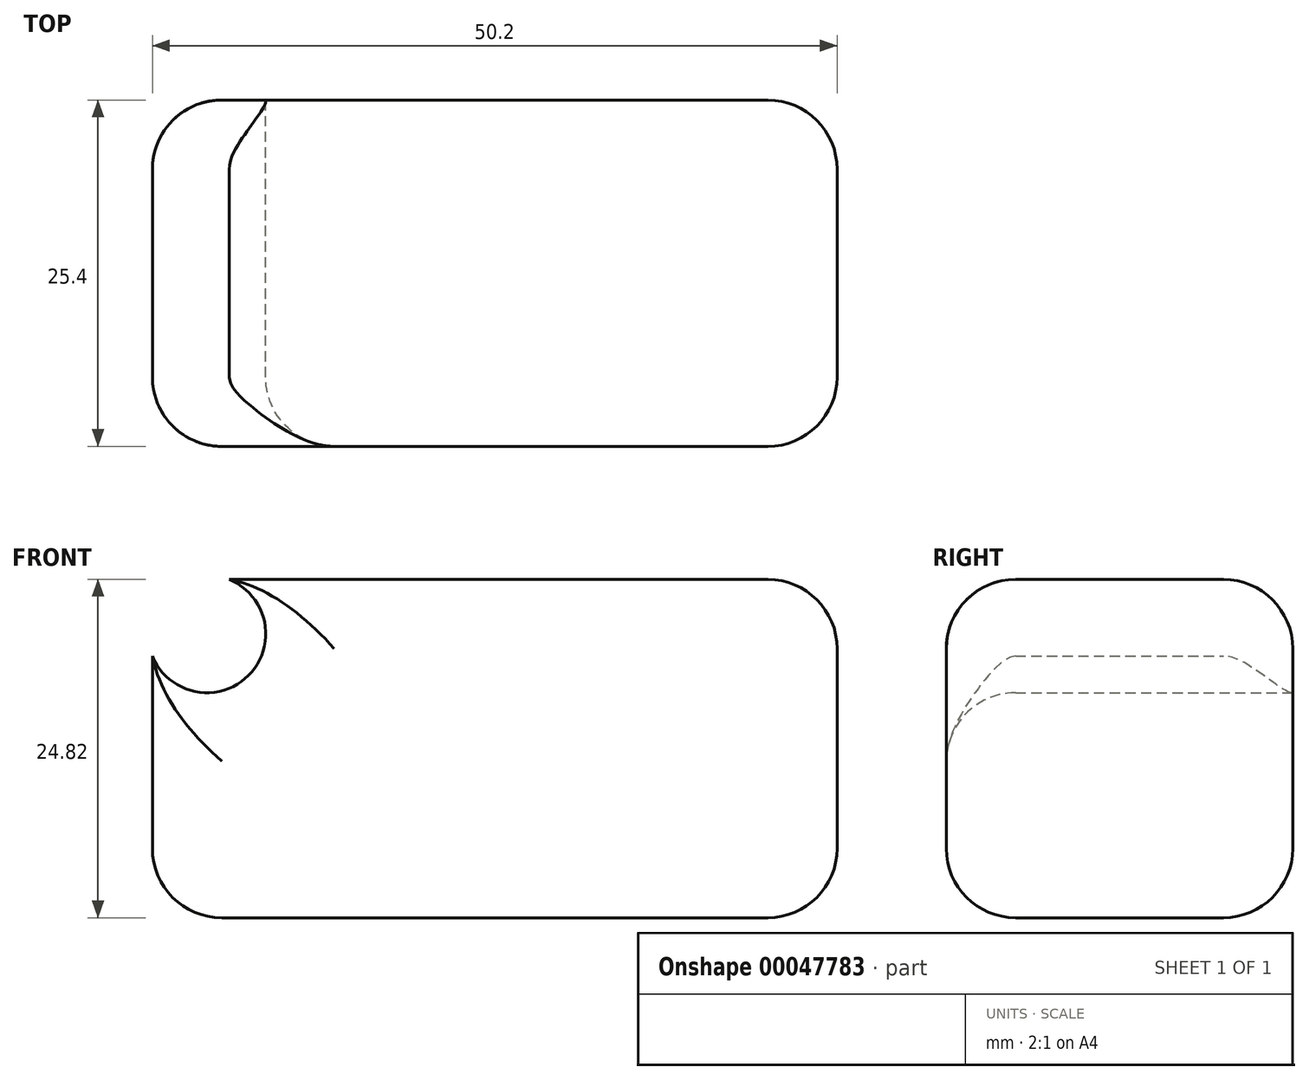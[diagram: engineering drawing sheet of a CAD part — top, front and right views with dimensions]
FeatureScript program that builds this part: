
annotation { "Feature Type Name" : "Feature", "Feature Type Description" : "" }
export const myFeature = defineFeature(function(context is Context, id is Id, definition is map)
    precondition{}
    {
        {
            var Q0;
            Q0=qCreatedBy(makeId("Front.planeOp"),FACE);
            var sketch = newSketch(context, id + "F0", { "sketchPlane" : qUnion([Q0])});
            skLineSegment(sketch, "E0.bottom", {"start": v(-47.06, 38.94) * mm, "end": v(3.14, 38.94) * mm});
            skLineSegment(sketch, "E0.top", {"start": v(-47.06, 14.12) * mm, "end": v(3.14, 14.12) * mm});
            skLineSegment(sketch, "E0.left", {"start": v(-47.06, 38.94) * mm, "end": v(-47.06, 14.12) * mm});
            skLineSegment(sketch, "E0.right", {"start": v(3.14, 38.94) * mm, "end": v(3.14, 14.12) * mm});
            skCircle(sketch, "E1", {"center": v(-43.07, 34.94) * mm, "radius": 4.32 * mm});
            skSolve(sketch);
        }
        {
            var Q0;
            {var subQ6=sQuery(id+"F0.wireOp",EDGE,"E0.top");Q0=makeQuery(id+"F0.imprint","IMPRINT",FACE,{"disambiguationData":[TD([[makeQuery(id+"F0.imprint","IMPRINT",EDGE,{"derivedFrom":subQ6}),1.0]])]});}
            extrude(context, id + "F1", {"entities" : qUnion([Q0]), "depth" : 25.4 * mm});
        }
        {
            var Q0;
            Q0=makeQuery(id+"F1.opExtrude","CAP_EDGE",EDGE,{"disambiguationData":[OSD([sQuery(id+"F0.wireOp",EDGE,"E0.bottom")])],"isStart":false});
            var Q1;
            Q1=makeQuery(id+"F1.opExtrude","CAP_FACE",FACE,{"disambiguationData":[OSD([sQuery(id+"F0.wireOp",EDGE,"E0.bottom"),sQuery(id+"F0.wireOp",EDGE,"E0.top"),sQuery(id+"F0.wireOp",EDGE,"E0.left"),sQuery(id+"F0.wireOp",EDGE,"E0.right"),sQuery(id+"F0.wireOp",EDGE,"E1")])],"isStart":false});
            var Q2;
            Q2=makeQuery(id+"F1.opExtrude","CAP_FACE",FACE,{"disambiguationData":[OSD([sQuery(id+"F0.wireOp",EDGE,"E0.bottom"),sQuery(id+"F0.wireOp",EDGE,"E0.top"),sQuery(id+"F0.wireOp",EDGE,"E0.left"),sQuery(id+"F0.wireOp",EDGE,"E0.right"),sQuery(id+"F0.wireOp",EDGE,"E1")])],"isStart":false});
            var Q3;
            Q3=makeQuery(id+"F1.opExtrude","CAP_EDGE",EDGE,{"disambiguationData":[OSD([sQuery(id+"F0.wireOp",EDGE,"E0.top")])],"isStart":true});
            var Q4;
            Q4=makeQuery(id+"F1.opExtrude","CAP_EDGE",EDGE,{"disambiguationData":[OSD([sQuery(id+"F0.wireOp",EDGE,"E0.right")])],"isStart":true});
            var Q5;
            Q5=makeQuery(id+"F1.opExtrude","CAP_EDGE",EDGE,{"disambiguationData":[OSD([sQuery(id+"F0.wireOp",EDGE,"E0.left")])],"isStart":true});
            var Q6;
            Q6=makeQuery(id+"F1.opExtrude","SWEPT_EDGE",EDGE,{"disambiguationData":[OSD([sQuery(id+"F0.wireOp",EDGE,"E0.top"),sQuery(id+"F0.wireOp",EDGE,"E0.left")])]});
            fillet(context, id + "F2", {"entities" : qUnion([Q0, Q1, Q2, Q3, Q4, Q5, Q6]), "radius" : 5.08 * mm, "tangentPropagation" : true, "allowEdgeOverflow" : false});
        }
        {
            var Q0;
            Q0=makeQuery(id+"F1.opExtrude","SWEPT_EDGE",EDGE,{"disambiguationData":[OSD([sQuery(id+"F0.wireOp",EDGE,"E0.bottom"),sQuery(id+"F0.wireOp",EDGE,"E0.right")])]});
            fillet(context, id + "F3", {"entities" : qUnion([Q0]), "radius" : 5.08 * mm, "tangentPropagation" : true, "allowEdgeOverflow" : false});
        }
        {
            var Q0;
            Q0=makeQuery(id+"F1.opExtrude","SWEPT_EDGE",EDGE,{"disambiguationData":[OSD([sQuery(id+"F0.wireOp",EDGE,"E0.top"),sQuery(id+"F0.wireOp",EDGE,"E0.right")])]});
            fillet(context, id + "F4", {"entities" : qUnion([Q0]), "radius" : 5.08 * mm, "tangentPropagation" : true, "allowEdgeOverflow" : false});
        }
    });
